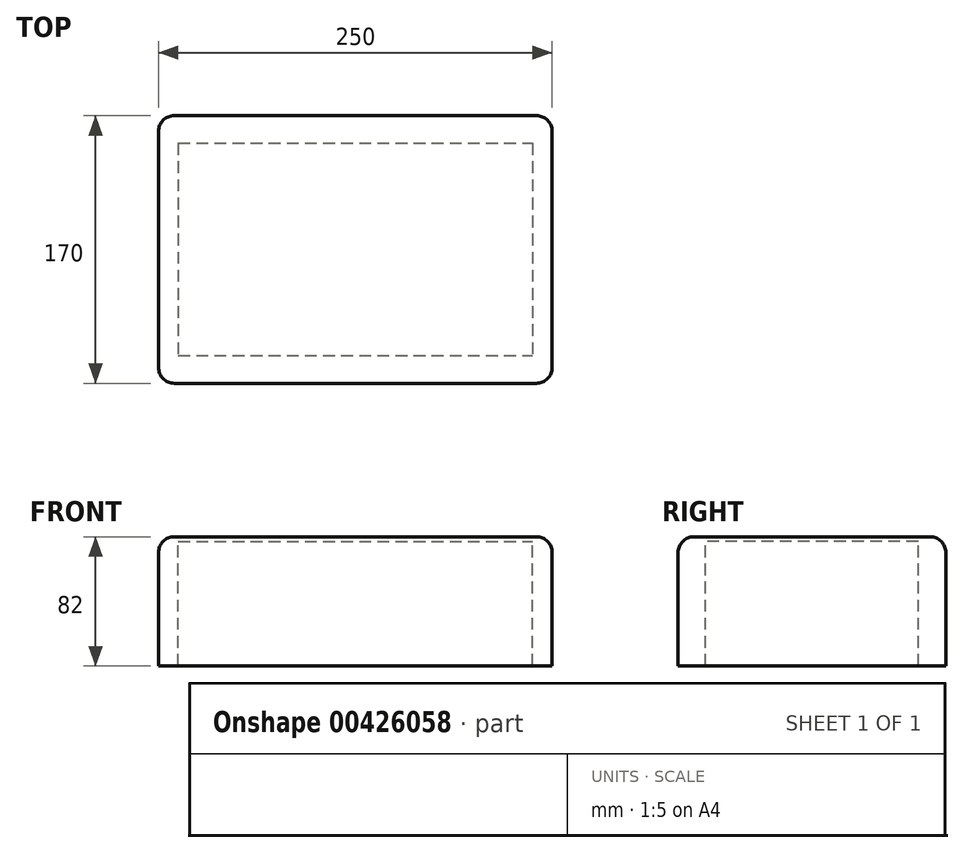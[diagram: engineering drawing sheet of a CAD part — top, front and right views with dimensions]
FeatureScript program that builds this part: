
annotation { "Feature Type Name" : "Feature", "Feature Type Description" : "" }
export const myFeature = defineFeature(function(context is Context, id is Id, definition is map)
    precondition{}
    {
        {
            var Q0;
            Q0=qCreatedBy(makeId("Top.planeOp"),FACE);
            var sketch = newSketch(context, id + "F0", { "sketchPlane" : qUnion([Q0])});
            skLineSegment(sketch, "E0.bottom", {"start": v(125, -85) * mm, "end": v(-125, -85) * mm});
            skLineSegment(sketch, "E0.top", {"start": v(125, 85) * mm, "end": v(-125, 85) * mm});
            skLineSegment(sketch, "E0.left", {"start": v(125, -85) * mm, "end": v(125, 85) * mm});
            skLineSegment(sketch, "E0.right", {"start": v(-125, -85) * mm, "end": v(-125, 85) * mm});
            skPoint(sketch, "E0.middle", {"position": v(0, 0) * mm});
            skLineSegment(sketch, "E1.bottom", {"start": v(117.5, -75) * mm, "end": v(-117.5, -75) * mm});
            skLineSegment(sketch, "E1.top", {"start": v(117.5, 75) * mm, "end": v(-117.5, 75) * mm});
            skLineSegment(sketch, "E1.left", {"start": v(117.5, -75) * mm, "end": v(117.5, 75) * mm});
            skLineSegment(sketch, "E1.right", {"start": v(-117.5, -75) * mm, "end": v(-117.5, 75) * mm});
            skSolve(sketch);
        }
        {
            var Q0;
            Q0=makeQuery(id+"F0.imprint","IMPRINT",FACE,{"disambiguationData":[TD([[makeQuery(id+"F0.imprint","IMPRINT",EDGE,{"derivedFrom":sQuery(id+"F0.wireOp",EDGE,"E1.bottom")}),-1.0]])]});
            var Q1;
            Q1=makeQuery(id+"F0.imprint","IMPRINT",FACE,{"disambiguationData":[TD([[makeQuery(id+"F0.imprint","IMPRINT",EDGE,{"derivedFrom":sQuery(id+"F0.wireOp",EDGE,"E0.bottom")}),-1.0]])]});
            extrude(context, id + "F1", {"entities" : qUnion([Q0, Q1]), "depth" : 3 * mm});
        }
        {
            var Q0;
            Q0=makeQuery(id+"F1.opExtrude","CAP_FACE",FACE,{"disambiguationData":[OSD([sQuery(id+"F0.wireOp",EDGE,"E0.bottom"),sQuery(id+"F0.wireOp",EDGE,"E0.top"),sQuery(id+"F0.wireOp",EDGE,"E0.left"),sQuery(id+"F0.wireOp",EDGE,"E0.right")])],"isStart":false});
            var sketch = newSketch(context, id + "F2", { "sketchPlane" : qUnion([Q0])});
            skLineSegment(sketch, "E2.bottom", {"start": v(-112.5, 67.5) * mm, "end": v(112.5, 67.5) * mm});
            skLineSegment(sketch, "E2.top", {"start": v(-112.5, -67.5) * mm, "end": v(112.5, -67.5) * mm});
            skLineSegment(sketch, "E2.left", {"start": v(-112.5, 67.5) * mm, "end": v(-112.5, -67.5) * mm});
            skLineSegment(sketch, "E2.right", {"start": v(112.5, 67.5) * mm, "end": v(112.5, -67.5) * mm});
            skPoint(sketch, "E2.middle", {"position": v(0, 0) * mm});
            skSolve(sketch);
        }
        {
            var Q0;
            Q0=makeQuery(id+"F2.imprint","IMPRINT",FACE,{"disambiguationData":[TD([[makeQuery(id+"F2.imprint","IMPRINT",EDGE,{"derivedFrom":sQuery(id+"F2.wireOp",EDGE,"E2.bottom")}),1.0]])]});
            extrude(context, id + "F3", {"entities" : qUnion([Q0]), "operationType" : NewBodyOperationType.ADD, "oppositeDirection" : true, "depth" : 82 * mm});
        }
        {
            var Q0;
            Q0=makeQuery(id+"F1.opExtrude","CAP_EDGE",EDGE,{"disambiguationData":[OSD([sQuery(id+"F0.wireOp",EDGE,"E0.right")])],"isStart":false});
            var Q1;
            Q1=makeQuery(id+"F1.opExtrude","CAP_EDGE",EDGE,{"disambiguationData":[OSD([sQuery(id+"F0.wireOp",EDGE,"E0.bottom")])],"isStart":false});
            var Q2;
            Q2=makeQuery(id+"F1.opExtrude","CAP_EDGE",EDGE,{"disambiguationData":[OSD([sQuery(id+"F0.wireOp",EDGE,"E0.left")])],"isStart":false});
            var Q3;
            Q3=makeQuery(id+"F1.opExtrude","CAP_EDGE",EDGE,{"disambiguationData":[OSD([sQuery(id+"F0.wireOp",EDGE,"E0.top")])],"isStart":false});
            var Q4;
            {var subQ0=sQuery(id+"F0.wireOp",EDGE,"E0.left");var subQ1=sQuery(id+"F0.wireOp",EDGE,"E0.bottom");Q4=makeQuery(id+"F3.boolean.opBoolean","MERGE",EDGE,{"derivedFrom":[makeQuery(id+"F1.opExtrude","SWEPT_EDGE",EDGE,{"disambiguationData":[OSD([subQ1,subQ0])]}),makeQuery(id+"F3.opExtrude","SWEPT_EDGE",EDGE,{"disambiguationData":[OSD([subQ1,subQ0])]})]});}
            var Q5;
            {var subQ0=sQuery(id+"F0.wireOp",EDGE,"E0.left");var subQ1=sQuery(id+"F0.wireOp",EDGE,"E0.top");Q5=makeQuery(id+"F3.boolean.opBoolean","MERGE",EDGE,{"derivedFrom":[makeQuery(id+"F1.opExtrude","SWEPT_EDGE",EDGE,{"disambiguationData":[OSD([subQ1,subQ0])]}),makeQuery(id+"F3.opExtrude","SWEPT_EDGE",EDGE,{"disambiguationData":[OSD([subQ1,subQ0])]})]});}
            var Q6;
            {var subQ0=sQuery(id+"F0.wireOp",EDGE,"E0.right");var subQ1=sQuery(id+"F0.wireOp",EDGE,"E0.bottom");Q6=makeQuery(id+"F3.boolean.opBoolean","MERGE",EDGE,{"derivedFrom":[makeQuery(id+"F1.opExtrude","SWEPT_EDGE",EDGE,{"disambiguationData":[OSD([subQ1,subQ0])]}),makeQuery(id+"F3.opExtrude","SWEPT_EDGE",EDGE,{"disambiguationData":[OSD([subQ1,subQ0])]})]});}
            var Q7;
            {var subQ0=sQuery(id+"F0.wireOp",EDGE,"E0.right");var subQ1=sQuery(id+"F0.wireOp",EDGE,"E0.top");Q7=makeQuery(id+"F3.boolean.opBoolean","MERGE",EDGE,{"derivedFrom":[makeQuery(id+"F1.opExtrude","SWEPT_EDGE",EDGE,{"disambiguationData":[OSD([subQ1,subQ0])]}),makeQuery(id+"F3.opExtrude","SWEPT_EDGE",EDGE,{"disambiguationData":[OSD([subQ1,subQ0])]})]});}
            fillet(context, id + "F4", {"entities" : qUnion([Q0, Q1, Q2, Q3, Q4, Q5, Q6, Q7]), "radius" : 10 * mm, "tangentPropagation" : true, "allowEdgeOverflow" : false});
        }
    });
